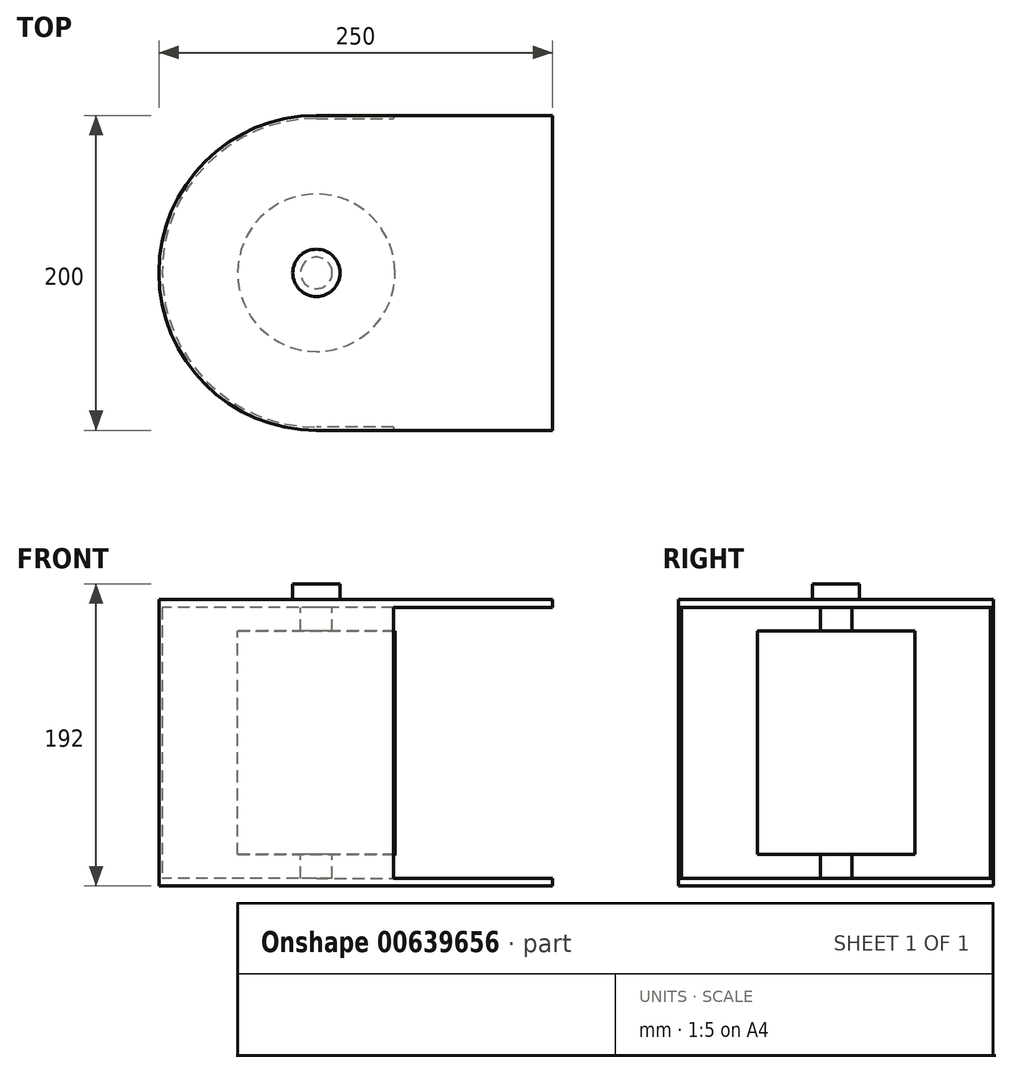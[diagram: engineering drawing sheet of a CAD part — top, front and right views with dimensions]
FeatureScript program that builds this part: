
annotation { "Feature Type Name" : "Feature", "Feature Type Description" : "" }
export const myFeature = defineFeature(function(context is Context, id is Id, definition is map)
    precondition{}
    {
        {
            var Q0;
            Q0=qCreatedBy(makeId("Front.planeOp"),FACE);
            var sketch = newSketch(context, id + "F0", { "sketchPlane" : qUnion([Q0])});
            skLineSegment(sketch, "E0", {"start": v(0, 78.5) * mm, "end": v(10, 78.5) * mm});
            skLineSegment(sketch, "E1", {"start": v(10, 78.5) * mm, "end": v(10, 63.5) * mm});
            skLineSegment(sketch, "E2", {"start": v(10, 63.5) * mm, "end": v(50, 63.5) * mm});
            skLineSegment(sketch, "E3", {"start": v(50, 63.5) * mm, "end": v(50, -78.5) * mm});
            skLineSegment(sketch, "E4", {"start": v(50, -78.5) * mm, "end": v(10, -78.5) * mm});
            skLineSegment(sketch, "E5", {"start": v(10, -78.5) * mm, "end": v(10, -93.5) * mm});
            skLineSegment(sketch, "E6", {"start": v(10, -93.5) * mm, "end": v(0, -93.5) * mm});
            skLineSegment(sketch, "E7", {"start": v(0, -93.5) * mm, "end": v(0, 78.5) * mm});
            skSolve(sketch);
        }
        {
            var Q0;
            Q0=qCreatedBy(makeId("Front.planeOp"),FACE);
            var sketch = newSketch(context, id + "F1", { "sketchPlane" : qUnion([Q0])});
            skLineSegment(sketch, "E8", {"start": v(0, 83.7) * mm, "end": v(0, -88.14) * mm});
            skSolve(sketch);
        }
        {
            var Q0;
            Q0 = qSketchRegion(id + "F0", true);
            var Q1;
            Q1=sQuery(id+"F1.wireOp",EDGE,"E8");
            revolve(context, id + "F2", {"entities" : qUnion([Q0]), "axis" : qUnion([Q1]), "revolveType" : RevolveType.FULL});
        }
        {
            var Q0;
            Q0=makeQuery(id+"F2.opRevolve","SWEPT_FACE",FACE,{"disambiguationData":[OSD([sQuery(id+"F0.wireOp",EDGE,"E0")])]});
            var sketch = newSketch(context, id + "F3", { "sketchPlane" : qUnion([Q0])});
            skArc(sketch, "E9", {"start": v(0, 100) * mm, "mid": v(-100, 0) * mm, "end": v(0, -100) * mm});
            skLineSegment(sketch, "E10", {"start": v(0, 100) * mm, "end": v(150, 100) * mm});
            skLineSegment(sketch, "E11", {"start": v(150, 100) * mm, "end": v(150, -100) * mm});
            skLineSegment(sketch, "E12", {"start": v(150, -100) * mm, "end": v(0, -100) * mm});
            skSolve(sketch);
        }
        {
            var Q0;
            Q0 = qSketchRegion(id + "F3", true);
            extrude(context, id + "F4", {"entities" : qUnion([Q0]), "operationType" : NewBodyOperationType.ADD, "depth" : 5 * mm, "offsetDistance" : 25 * mm});
        }
        {
            var Q0;
            Q0=makeQuery(id+"F2.opRevolve","SWEPT_FACE",FACE,{"disambiguationData":[OSD([sQuery(id+"F0.wireOp",EDGE,"E6")])]});
            var sketch = newSketch(context, id + "F5", { "sketchPlane" : qUnion([Q0])});
            skArc(sketch, "E13.0", {"start": v(0, -100) * mm, "mid": v(-100, 0) * mm, "end": v(0, 100) * mm});
            skLineSegment(sketch, "E14.0", {"start": v(150, 100) * mm, "end": v(0, 100) * mm});
            skLineSegment(sketch, "E15.0", {"start": v(0, -100) * mm, "end": v(150, -100) * mm});
            skLineSegment(sketch, "E16.0", {"start": v(150, -100) * mm, "end": v(150, 100) * mm});
            skSolve(sketch);
        }
        {
            var Q0;
            Q0 = qSketchRegion(id + "F5", true);
            extrude(context, id + "F6", {"entities" : qUnion([Q0]), "operationType" : NewBodyOperationType.ADD, "depth" : 5 * mm, "offsetDistance" : 25 * mm});
        }
        {
            var Q0;
            Q0=makeQuery(id+"F6.opExtrude","CAP_FACE",FACE,{"disambiguationData":[OSD([sQuery(id+"F5.wireOp",EDGE,"E13.0"),sQuery(id+"F5.wireOp",EDGE,"E14.0"),sQuery(id+"F5.wireOp",EDGE,"E15.0"),sQuery(id+"F5.wireOp",EDGE,"E16.0")])],"isStart":true});
            var sketch = newSketch(context, id + "F7", { "sketchPlane" : qUnion([Q0])});
            skArc(sketch, "E17.0", {"start": v(0, 100) * mm, "mid": v(-100, 0) * mm, "end": v(0, -100) * mm});
            skLineSegment(sketch, "E18.0", {"start": v(49, -100) * mm, "end": v(0, -100) * mm});
            skLineSegment(sketch, "E19.0", {"start": v(0, 100) * mm, "end": v(49, 100) * mm});
            skLineSegment(sketch, "E20.0", {"start": v(0, 98) * mm, "end": v(49, 98) * mm});
            skArc(sketch, "E20.1", {"start": v(0, 98) * mm, "mid": v(-98, 0) * mm, "end": v(0, -98) * mm});
            skLineSegment(sketch, "E20.2", {"start": v(49, -98) * mm, "end": v(0, -98) * mm});
            skLineSegment(sketch, "E21", {"start": v(49, 100) * mm, "end": v(49, 98) * mm});
            skPoint(sketch, "E22.orphan", {"position": v(150, 100) * mm});
            skPoint(sketch, "E23.orphan", {"position": v(150, -100) * mm});
            skLineSegment(sketch, "E24.trimOffspring", {"start": v(49, -98) * mm, "end": v(49, -100) * mm});
            skSolve(sketch);
        }
        {
            var Q0;
            Q0 = qSketchRegion(id + "F7", true);
            var Q1;
            Q1=makeQuery(id+"F4.opExtrude","CAP_FACE",FACE,{"disambiguationData":[OSD([sQuery(id+"F3.wireOp",EDGE,"E9"),sQuery(id+"F3.wireOp",EDGE,"E10"),sQuery(id+"F3.wireOp",EDGE,"E11"),sQuery(id+"F3.wireOp",EDGE,"E12")])],"isStart":true});
            extrude(context, id + "F8", {"entities" : qUnion([Q0]), "operationType" : NewBodyOperationType.ADD, "endBound" : BoundingType.UP_TO_SURFACE, "depth" : 25 * mm, "endBoundEntityFace" : qUnion([Q1]), "offsetDistance" : 25 * mm});
        }
        {
            var Q0;
            Q0=makeQuery(id+"F4.opExtrude","CAP_FACE",FACE,{"disambiguationData":[OSD([sQuery(id+"F3.wireOp",EDGE,"E9"),sQuery(id+"F3.wireOp",EDGE,"E10"),sQuery(id+"F3.wireOp",EDGE,"E11"),sQuery(id+"F3.wireOp",EDGE,"E12")])],"isStart":false});
            var sketch = newSketch(context, id + "F9", { "sketchPlane" : qUnion([Q0])});
            skCircle(sketch, "E25", {"center": v(0, 0) * mm, "radius": 15 * mm});
            skSolve(sketch);
        }
        {
            var Q0;
            Q0 = qSketchRegion(id + "F9", true);
            extrude(context, id + "F10", {"entities" : qUnion([Q0]), "operationType" : NewBodyOperationType.ADD, "depth" : 10 * mm, "offsetDistance" : 25 * mm});
        }
    });
